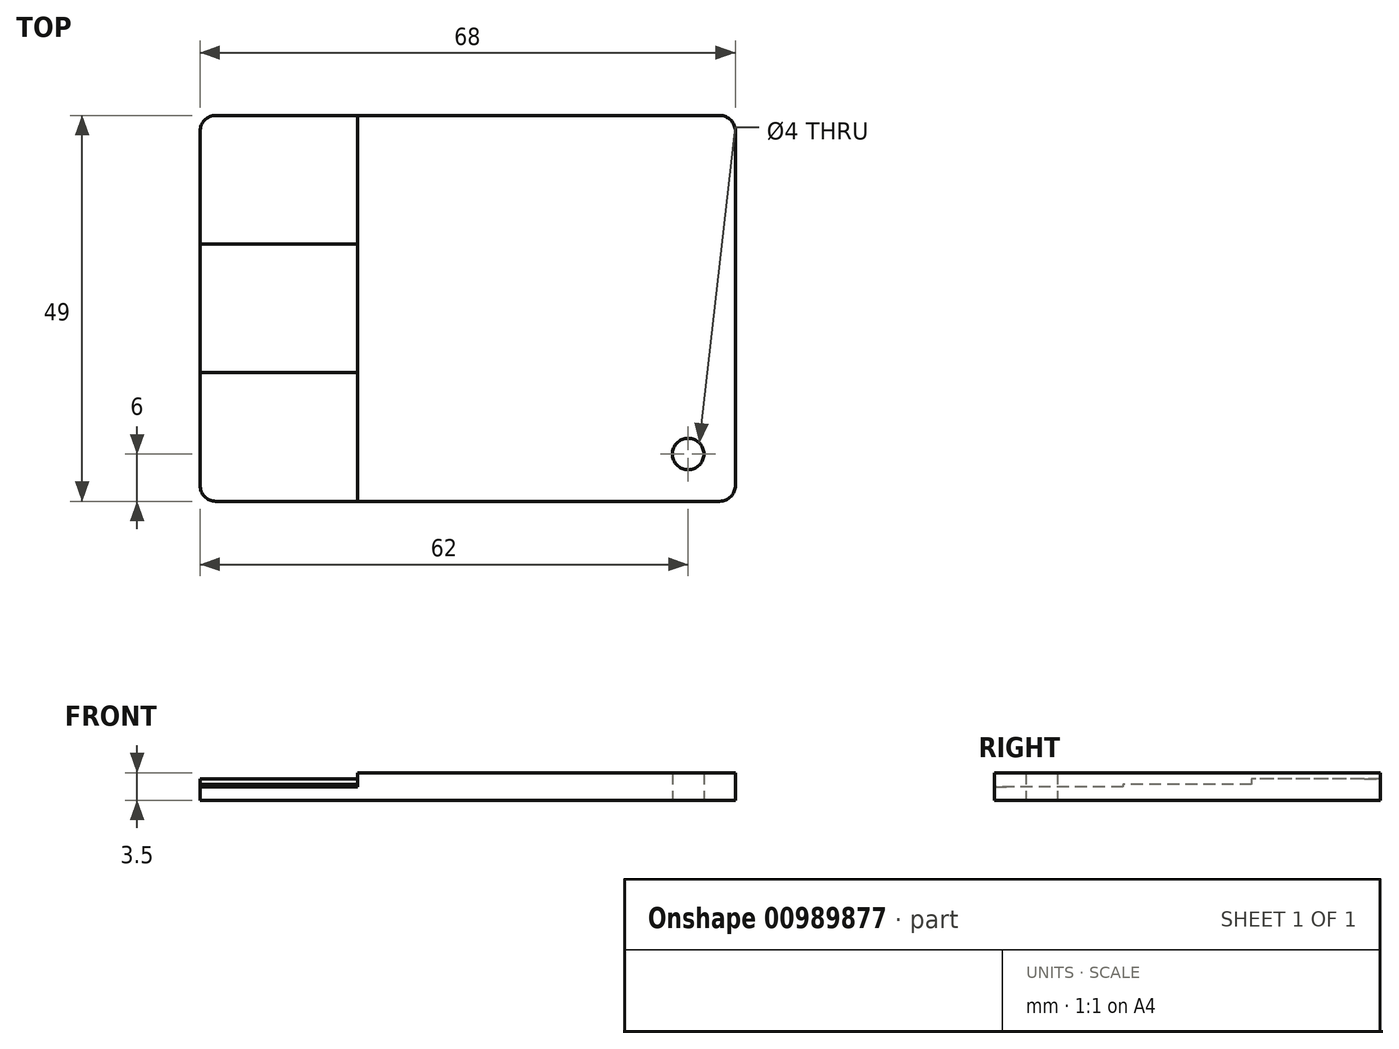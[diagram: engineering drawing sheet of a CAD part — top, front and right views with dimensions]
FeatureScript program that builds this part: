
annotation { "Feature Type Name" : "Feature", "Feature Type Description" : "" }
export const myFeature = defineFeature(function(context is Context, id is Id, definition is map)
    precondition{}
    {
        {
            var Q0;
            Q0=qCreatedBy(makeId("Top.planeOp"),FACE);
            var sketch = newSketch(context, id + "F0", { "sketchPlane" : qUnion([Q0])});
            skLineSegment(sketch, "E0.bottom", {"start": v(34, -24.5) * mm, "end": v(-34, -24.5) * mm});
            skLineSegment(sketch, "E0.top", {"start": v(34, 24.5) * mm, "end": v(-34, 24.5) * mm});
            skLineSegment(sketch, "E0.left", {"start": v(34, -24.5) * mm, "end": v(34, 24.5) * mm});
            skLineSegment(sketch, "E0.right", {"start": v(-34, -24.5) * mm, "end": v(-34, 24.5) * mm});
            skPoint(sketch, "E0.middle", {"position": v(0, 0) * mm});
            skSolve(sketch);
        }
        {
            var Q0;
            Q0 = qSketchRegion(id + "F0", true);
            extrude(context, id + "F1", {"entities" : qUnion([Q0]), "depth" : 3.5 * mm, "offsetDistance" : 25.4 * mm});
        }
        {
            var Q0;
            Q0=makeQuery(id+"F1.opExtrude","SWEPT_FACE",FACE,{"disambiguationData":[OSD([sQuery(id+"F0.wireOp",EDGE,"E0.right")])]});
            var sketch = newSketch(context, id + "F2", { "sketchPlane" : qUnion([Q0])});
            skLineSegment(sketch, "E1", {"start": v(-24.5, 3.5) * mm, "end": v(-24.5, 2.7) * mm});
            skLineSegment(sketch, "E2", {"start": v(-24.5, 2.7) * mm, "end": v(-8.17, 2.7) * mm});
            skLineSegment(sketch, "E3", {"start": v(-8.17, 2.7) * mm, "end": v(-8.17, 2) * mm});
            skLineSegment(sketch, "E4", {"start": v(-8.17, 2) * mm, "end": v(8.17, 2) * mm});
            skLineSegment(sketch, "E5", {"start": v(8.17, 2) * mm, "end": v(8.17, 1.7) * mm});
            skLineSegment(sketch, "E6", {"start": v(8.17, 1.7) * mm, "end": v(24.5, 1.7) * mm});
            skLineSegment(sketch, "E7", {"start": v(24.5, 1.7) * mm, "end": v(24.5, 3.5) * mm});
            skLineSegment(sketch, "E8", {"start": v(24.5, 3.5) * mm, "end": v(-24.5, 3.5) * mm});
            skSolve(sketch);
        }
        {
            var Q0;
            Q0 = qSketchRegion(id + "F2", true);
            extrude(context, id + "F3", {"entities" : qUnion([Q0]), "operationType" : NewBodyOperationType.REMOVE, "oppositeDirection" : true, "depth" : 20 * mm, "offsetDistance" : 25.4 * mm});
        }
        {
            var Q0;
            Q0=qCreatedBy(makeId("Top.planeOp"),FACE);
            var sketch = newSketch(context, id + "F4", { "sketchPlane" : qUnion([Q0])});
            skCircle(sketch, "E9", {"center": v(28, -18.5) * mm, "radius": 2 * mm});
            skSolve(sketch);
        }
        {
            var Q0;
            Q0 = qSketchRegion(id + "F4", true);
            extrude(context, id + "F5", {"entities" : qUnion([Q0]), "operationType" : NewBodyOperationType.REMOVE, "endBound" : BoundingType.THROUGH_ALL, "depth" : 25.4 * mm, "offsetDistance" : 25.4 * mm});
        }
        {
            var Q0;
            Q0=makeQuery(id+"F1.opExtrude","SWEPT_EDGE",EDGE,{"disambiguationData":[OSD([sQuery(id+"F0.wireOp",EDGE,"E0.top"),sQuery(id+"F0.wireOp",EDGE,"E0.left")])]});
            var Q1;
            Q1=makeQuery(id+"F1.opExtrude","SWEPT_EDGE",EDGE,{"disambiguationData":[OSD([sQuery(id+"F0.wireOp",EDGE,"E0.bottom"),sQuery(id+"F0.wireOp",EDGE,"E0.left")])]});
            var Q2;
            Q2=makeQuery(id+"F1.opExtrude","SWEPT_EDGE",EDGE,{"disambiguationData":[OSD([sQuery(id+"F0.wireOp",EDGE,"E0.top"),sQuery(id+"F0.wireOp",EDGE,"E0.right")])]});
            var Q3;
            Q3=makeQuery(id+"F1.opExtrude","SWEPT_EDGE",EDGE,{"disambiguationData":[OSD([sQuery(id+"F0.wireOp",EDGE,"E0.bottom"),sQuery(id+"F0.wireOp",EDGE,"E0.right")])]});
            fillet(context, id + "F6", {"entities" : qUnion([Q0, Q1, Q2, Q3]), "radius" : 2 * mm, "tangentPropagation" : true, "allowEdgeOverflow" : false});
        }
    });
